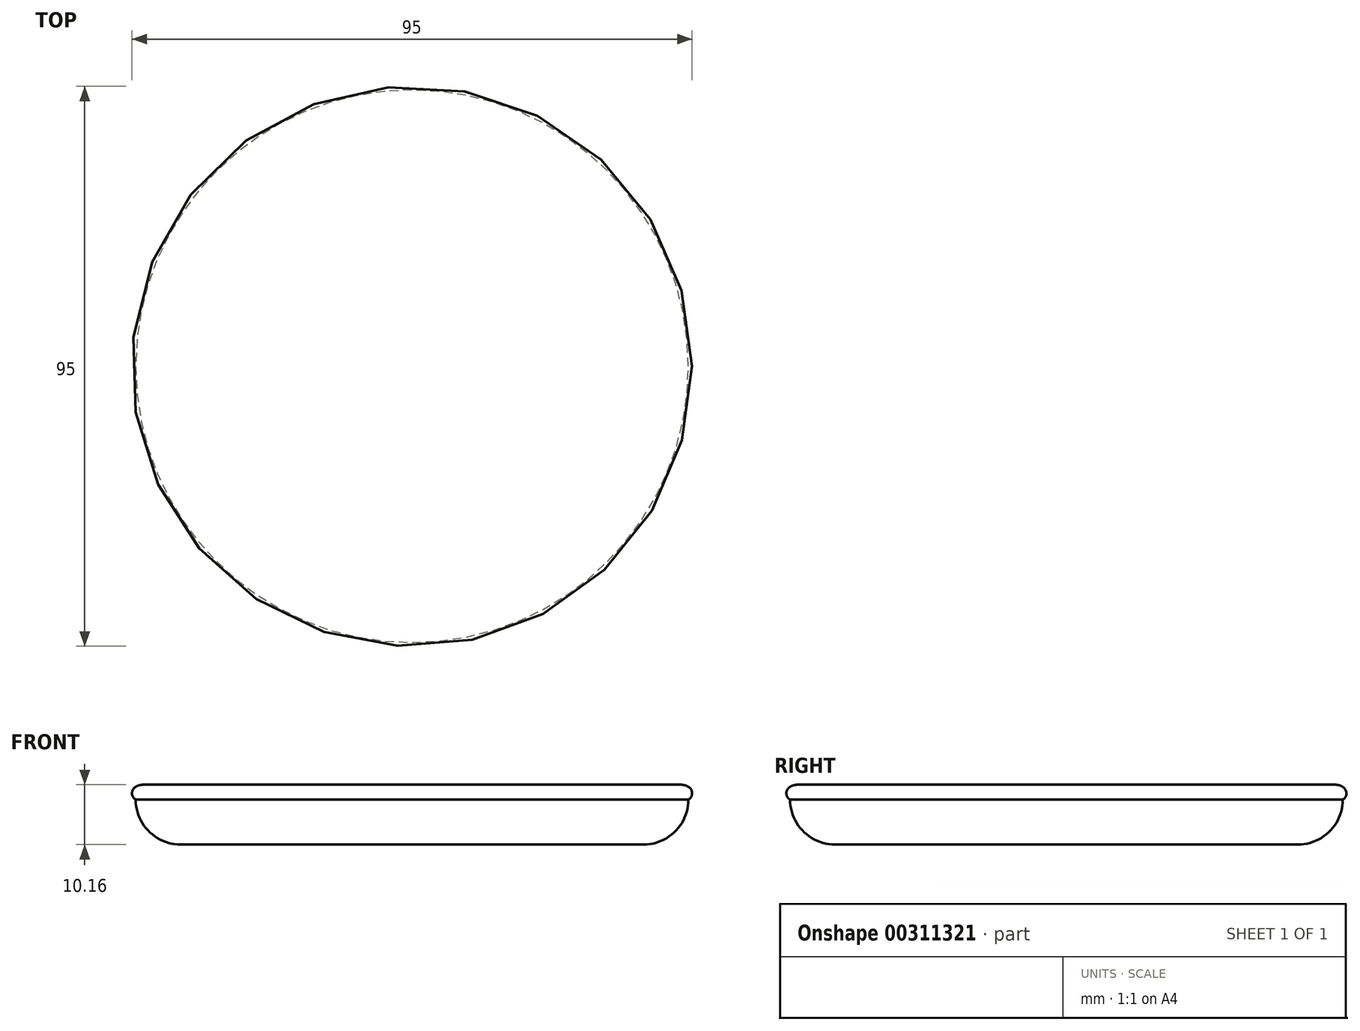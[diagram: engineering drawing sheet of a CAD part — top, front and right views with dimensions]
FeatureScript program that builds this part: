
annotation { "Feature Type Name" : "Feature", "Feature Type Description" : "" }
export const myFeature = defineFeature(function(context is Context, id is Id, definition is map)
    precondition{}
    {
        {
            var Q0;
            Q0=qCreatedBy(makeId("Top.planeOp"),FACE);
            var sketch = newSketch(context, id + "F0", { "sketchPlane" : qUnion([Q0])});
            skCircle(sketch, "E0", {"center": v(0, 0) * mm, "radius": 46.86 * mm});
            skSolve(sketch);
        }
        {
            var Q0;
            Q0=makeQuery(id+"F0.imprint","IMPRINT",FACE,{"disambiguationData":[TD([[makeQuery(id+"F0.imprint","IMPRINT",EDGE,{"derivedFrom":sQuery(id+"F0.wireOp",EDGE,"E0")}),1.0]])]});
            extrude(context, id + "F1", {"entities" : qUnion([Q0]), "depth" : 7.62 * mm});
        }
        {
            var Q0;
            Q0=makeQuery(id+"F1.opExtrude","CAP_FACE",FACE,{"disambiguationData":[OSD([sQuery(id+"F0.wireOp",EDGE,"E0")])],"isStart":false});
            var sketch = newSketch(context, id + "F2", { "sketchPlane" : qUnion([Q0])});
            skCircle(sketch, "E1", {"center": v(0, 0) * mm, "radius": 48.13 * mm});
            skSolve(sketch);
        }
        {
            var Q0;
            Q0 = qSketchRegion(id + "F2", true);
            extrude(context, id + "F3", {"entities" : qUnion([Q0]), "operationType" : NewBodyOperationType.ADD, "depth" : 2.54 * mm});
        }
        {
            var Q0;
            Q0=makeQuery(id+"F3.opExtrude","CAP_EDGE",EDGE,{"disambiguationData":[OSD([sQuery(id+"F2.wireOp",EDGE,"E1")])],"isStart":false});
            fillet(context, id + "F4", {"entities" : qUnion([Q0]), "radius" : 2.54 * mm, "tangentPropagation" : true, "allowEdgeOverflow" : false});
        }
        {
            var Q0;
            {var subQ0=sQuery(id+"F2.wireOp",EDGE,"E1");Q0=makeQuery(id+"F4.opFillet","BLEND_EDGE",EDGE,{"blendedFrom":[makeQuery(id+"F3.opExtrude","CAP_EDGE",EDGE,{"disambiguationData":[OSD([subQ0])],"isStart":false}),makeQuery(id+"F3.opExtrude","CAP_FACE",FACE,{"disambiguationData":[OSD([subQ0])],"isStart":true})],"blendedInto":[makeQuery(id+"F3.opExtrude","CAP_FACE",FACE,{"disambiguationData":[OSD([subQ0])],"isStart":true})]});}
            fillet(context, id + "F5", {"entities" : qUnion([Q0]), "radius" : 1.27 * mm, "tangentPropagation" : true, "allowEdgeOverflow" : false});
        }
        {
            var Q0;
            Q0=makeQuery(id+"F1.opExtrude","CAP_EDGE",EDGE,{"disambiguationData":[OSD([sQuery(id+"F0.wireOp",EDGE,"E0")])],"isStart":true});
            fillet(context, id + "F6", {"entities" : qUnion([Q0]), "radius" : 7.62 * mm, "tangentPropagation" : true, "allowEdgeOverflow" : false});
        }
    });
